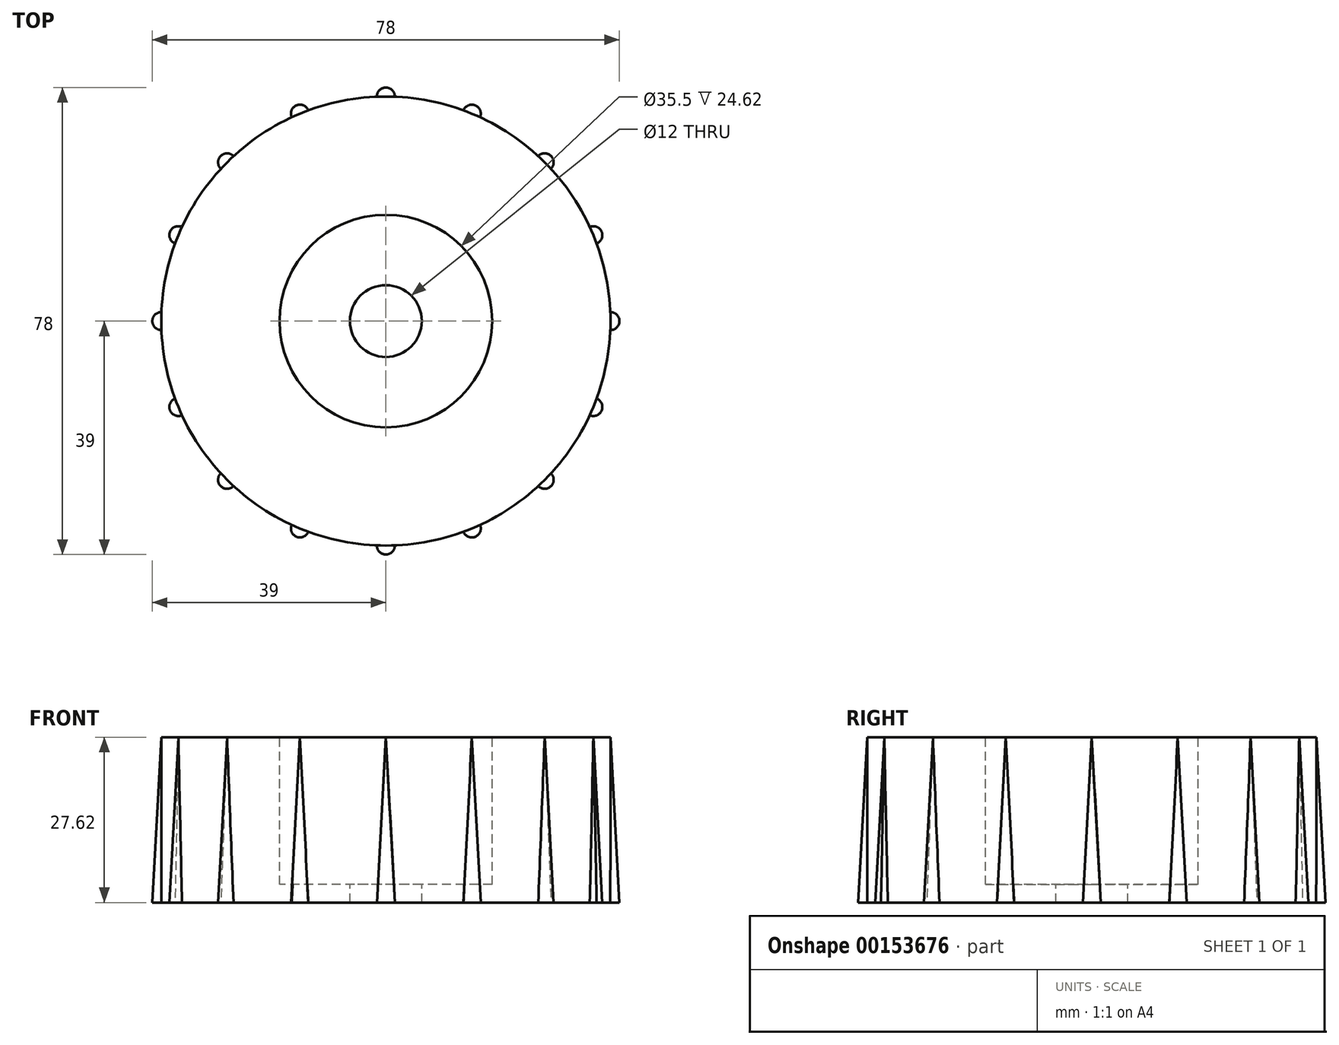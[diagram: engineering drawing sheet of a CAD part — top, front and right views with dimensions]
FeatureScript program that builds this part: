
annotation { "Feature Type Name" : "Feature", "Feature Type Description" : "" }
export const myFeature = defineFeature(function(context is Context, id is Id, definition is map)
    precondition{}
    {
        {
            var Q0;
            Q0=qCreatedBy(makeId("Top.planeOp"),FACE);
            var sketch = newSketch(context, id + "F0", { "sketchPlane" : qUnion([Q0])});
            skCircle(sketch, "E0", {"center": v(0, 0) * mm, "radius": 37.5 * mm});
            skSolve(sketch);
        }
        {
            var Q0;
            Q0 = qSketchRegion(id + "F0", true);
            extrude(context, id + "F1", {"entities" : qUnion([Q0]), "depth" : 27.62 * mm});
        }
        {
            var Q0;
            Q0=makeQuery(id+"F1.opExtrude","CAP_FACE",FACE,{"disambiguationData":[OSD([sQuery(id+"F0.wireOp",EDGE,"E0")])],"isStart":false});
            var sketch = newSketch(context, id + "F2", { "sketchPlane" : qUnion([Q0])});
            skCircle(sketch, "E1", {"center": v(0, 0) * mm, "radius": 17.75 * mm});
            skSolve(sketch);
        }
        {
            var Q0;
            Q0=makeQuery(id+"F2.imprint","IMPRINT",FACE,{"disambiguationData":[TD([[makeQuery(id+"F2.imprint","IMPRINT",EDGE,{"derivedFrom":sQuery(id+"F2.wireOp",EDGE,"E1")}),1.0]])]});
            extrude(context, id + "F3", {"entities" : qUnion([Q0]), "operationType" : NewBodyOperationType.REMOVE, "oppositeDirection" : true, "depth" : 24.62 * mm});
        }
        {
            var Q0;
            Q0=makeQuery(id+"F3.boolean.opBoolean","COPY",FACE,{"derivedFrom":makeQuery(id+"F3.opExtrude","CAP_FACE",FACE,{"disambiguationData":[OSD([sQuery(id+"F2.wireOp",EDGE,"E1")])],"isStart":false})});
            var sketch = newSketch(context, id + "F4", { "sketchPlane" : qUnion([Q0])});
            skCircle(sketch, "E2", {"center": v(0, 0) * mm, "radius": 6 * mm});
            skSolve(sketch);
        }
        {
            var Q0;
            Q0=makeQuery(id+"F4.imprint","IMPRINT",FACE,{"disambiguationData":[TD([[makeQuery(id+"F4.imprint","IMPRINT",EDGE,{"derivedFrom":sQuery(id+"F4.wireOp",EDGE,"E2")}),1.0]])]});
            extrude(context, id + "F5", {"entities" : qUnion([Q0]), "operationType" : NewBodyOperationType.REMOVE, "endBound" : BoundingType.THROUGH_ALL, "oppositeDirection" : true, "depth" : 25 * mm});
        }
        {
            var Q0;
            Q0=makeQuery(id+"F1.opExtrude","CAP_FACE",FACE,{"disambiguationData":[OSD([sQuery(id+"F0.wireOp",EDGE,"E0")])],"isStart":false});
            var sketch = newSketch(context, id + "F6", { "sketchPlane" : qUnion([Q0])});
            skPoint(sketch, "E3", {"position": v(-37.5, 0) * mm});
            skPoint(sketch, "E4.1.0", {"position": v(37.5, 0) * mm});
            skPoint(sketch, "E4.center", {"position": v(0, 0) * mm});
            skSolve(sketch);
        }
        {
            var Q0;
            Q0=qCreatedBy(makeId("Front.planeOp"),FACE);
            var sketch = newSketch(context, id + "F7", { "sketchPlane" : qUnion([Q0])});
            skLineSegment(sketch, "E5", {"start": v(-37.5, 27.62) * mm, "end": v(-39, 0) * mm});
            skLineSegment(sketch, "E6", {"start": v(-39, 0) * mm, "end": v(-37.5, 0) * mm});
            skLineSegment(sketch, "E7", {"start": v(-37.5, 0) * mm, "end": v(-37.5, 27.62) * mm});
            skSolve(sketch);
        }
        {
            var Q0;
            Q0=makeQuery(id+"F7.imprint","IMPRINT",FACE,{"disambiguationData":[TD([[makeQuery(id+"F7.imprint","IMPRINT",EDGE,{"derivedFrom":sQuery(id+"F7.wireOp",EDGE,"E5")}),1.0]])]});
            var Q1;
            Q1=sQuery(id+"F7.wireOp",EDGE,"E7");
            revolve(context, id + "F8", {"entities" : qUnion([Q0]), "axis" : qUnion([Q1]), "revolveType" : RevolveType.FULL});
        }
        {
            var Q0;
            Q0=qCreatedBy(makeId("Front.planeOp"),FACE);
            var sketch = newSketch(context, id + "F9", { "sketchPlane" : qUnion([Q0])});
            skLineSegment(sketch, "E8", {"start": v(0, 25.84) * mm, "end": v(0, 0) * mm, "construction": true});
            skSolve(sketch);
        }
        {
            var Q0;
            Q0=makeQuery(id+"F8.opRevolve","SWEPT_BODY",BODY,{"disambiguationData":[OSD([sQuery(id+"F7.wireOp",EDGE,"E5"),sQuery(id+"F7.wireOp",EDGE,"E6"),sQuery(id+"F7.wireOp",EDGE,"E7")])]});
            var Q1;
            Q1=sQuery(id+"F9.wireOp",EDGE,"E8");
            var Q2;
            Q2=makeQuery(id+"F1.opExtrude","SWEPT_BODY",BODY,{"disambiguationData":[OSD([sQuery(id+"F0.wireOp",EDGE,"E0")])]});
            circularPattern(context, id + "F10", {"operationType" : NewBodyOperationType.ADD, "entities" : qUnion([Q0]), "axis" : qUnion([Q1]), "angle" : 360 * degree, "instanceCount" : 16, "equalSpace" : true});
        }
    });
